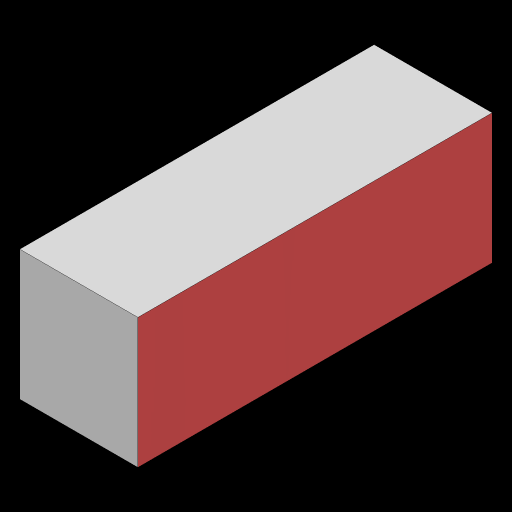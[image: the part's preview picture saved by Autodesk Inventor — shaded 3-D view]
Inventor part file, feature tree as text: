
AUTODESK INVENTOR PART (.ipt)
format: ipt  version: 2023.2 (Build 272271030, 271C)  size: 98,304 bytes
history: native  units: mm
features: extrude x1, sketch x1
ambient origin geometry x8: Origin, YZ Plane, XZ Plane, XY Plane, X Axis, Y Axis, Z Axis, Center Point
bodies: Solid1 (feature_tree)
feature tree (2):
  extrude  "Extrusion1"  Depth=11.0mm
  sketch  "Sketch1"  dims[d0=10.0mm d1=11.0mm d2=30.0mm d3=0.0mm]
